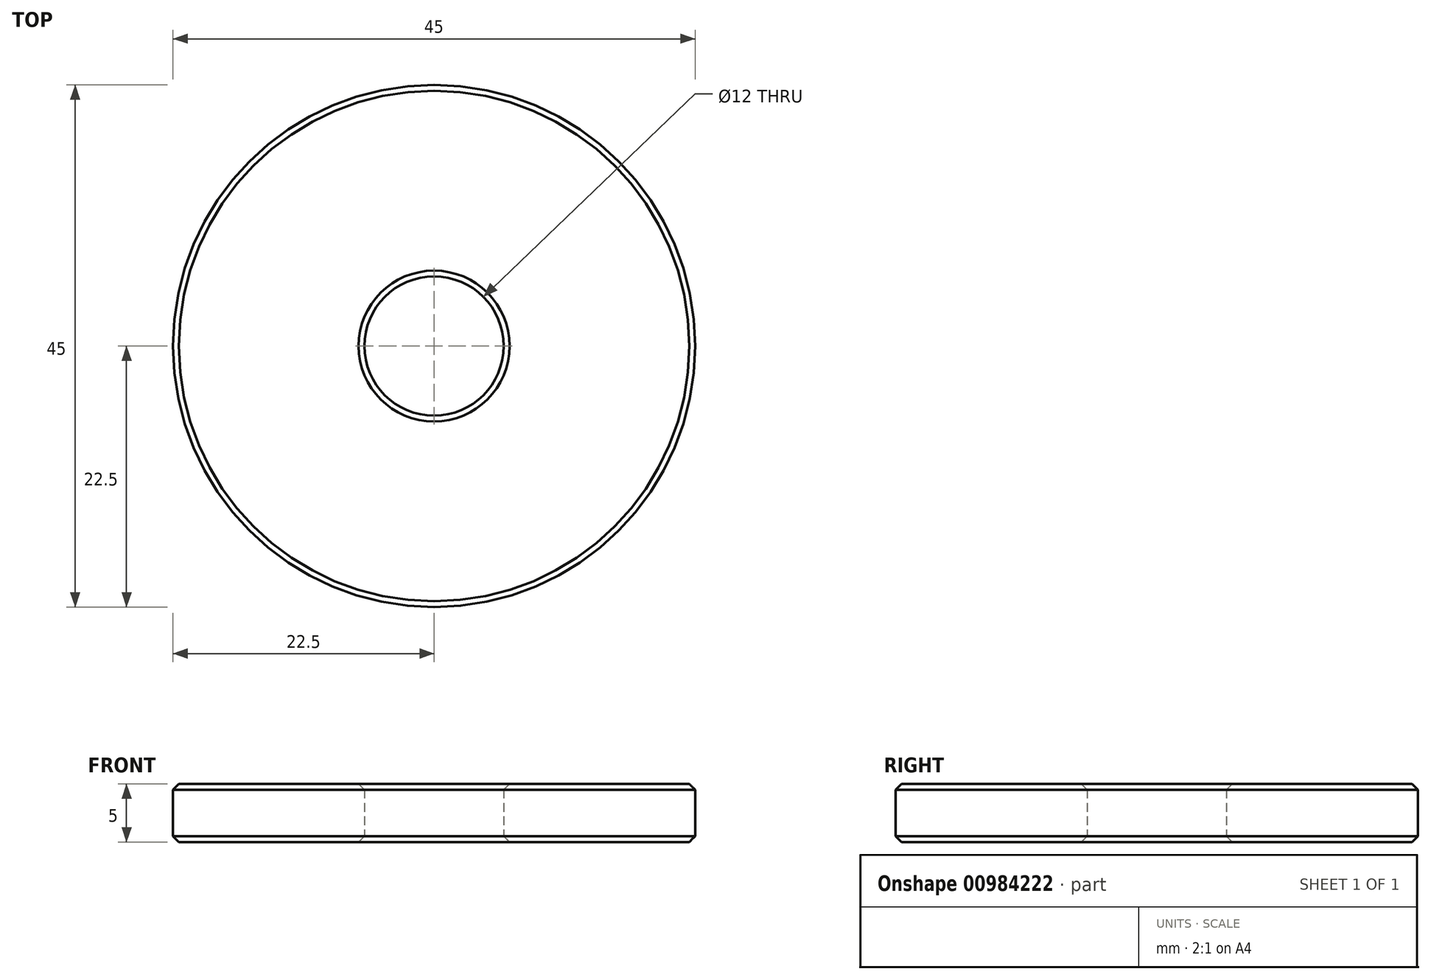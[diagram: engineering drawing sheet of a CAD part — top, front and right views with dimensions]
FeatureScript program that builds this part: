
annotation { "Feature Type Name" : "Feature", "Feature Type Description" : "" }
export const myFeature = defineFeature(function(context is Context, id is Id, definition is map)
    precondition{}
    {
        {
            var Q0;
            Q0=qCreatedBy(makeId("Top.planeOp"),FACE);
            var sketch = newSketch(context, id + "F0", { "sketchPlane" : qUnion([Q0])});
            skCircle(sketch, "E0", {"center": v(0, 0) * mm, "radius": 22.5 * mm});
            skCircle(sketch, "E1", {"center": v(0, 0) * mm, "radius": 6 * mm});
            skSolve(sketch);
        }
        {
            var Q0;
            Q0 = qSketchRegion(id + "F0", true);
            extrude(context, id + "F1", {"entities" : qUnion([Q0]), "depth" : 5 * mm, "offsetDistance" : 25 * mm});
        }
        {
            var Q0;
            Q0=makeQuery(id+"F1.opExtrude","CAP_EDGE",EDGE,{"disambiguationData":[OSD([sQuery(id+"F0.wireOp",EDGE,"E0")])],"isStart":true});
            var Q1;
            Q1=makeQuery(id+"F1.opExtrude","CAP_EDGE",EDGE,{"disambiguationData":[OSD([sQuery(id+"F0.wireOp",EDGE,"E1")])],"isStart":true});
            var Q2;
            Q2=makeQuery(id+"F1.opExtrude","CAP_EDGE",EDGE,{"disambiguationData":[OSD([sQuery(id+"F0.wireOp",EDGE,"E1")])],"isStart":false});
            var Q3;
            Q3=makeQuery(id+"F1.opExtrude","CAP_EDGE",EDGE,{"disambiguationData":[OSD([sQuery(id+"F0.wireOp",EDGE,"E0")])],"isStart":false});
            chamfer(context, id + "F2", {"entities" : qUnion([Q0, Q1, Q2, Q3]), "width" : .5 * mm, "tangentPropagation" : true});
        }
    });
